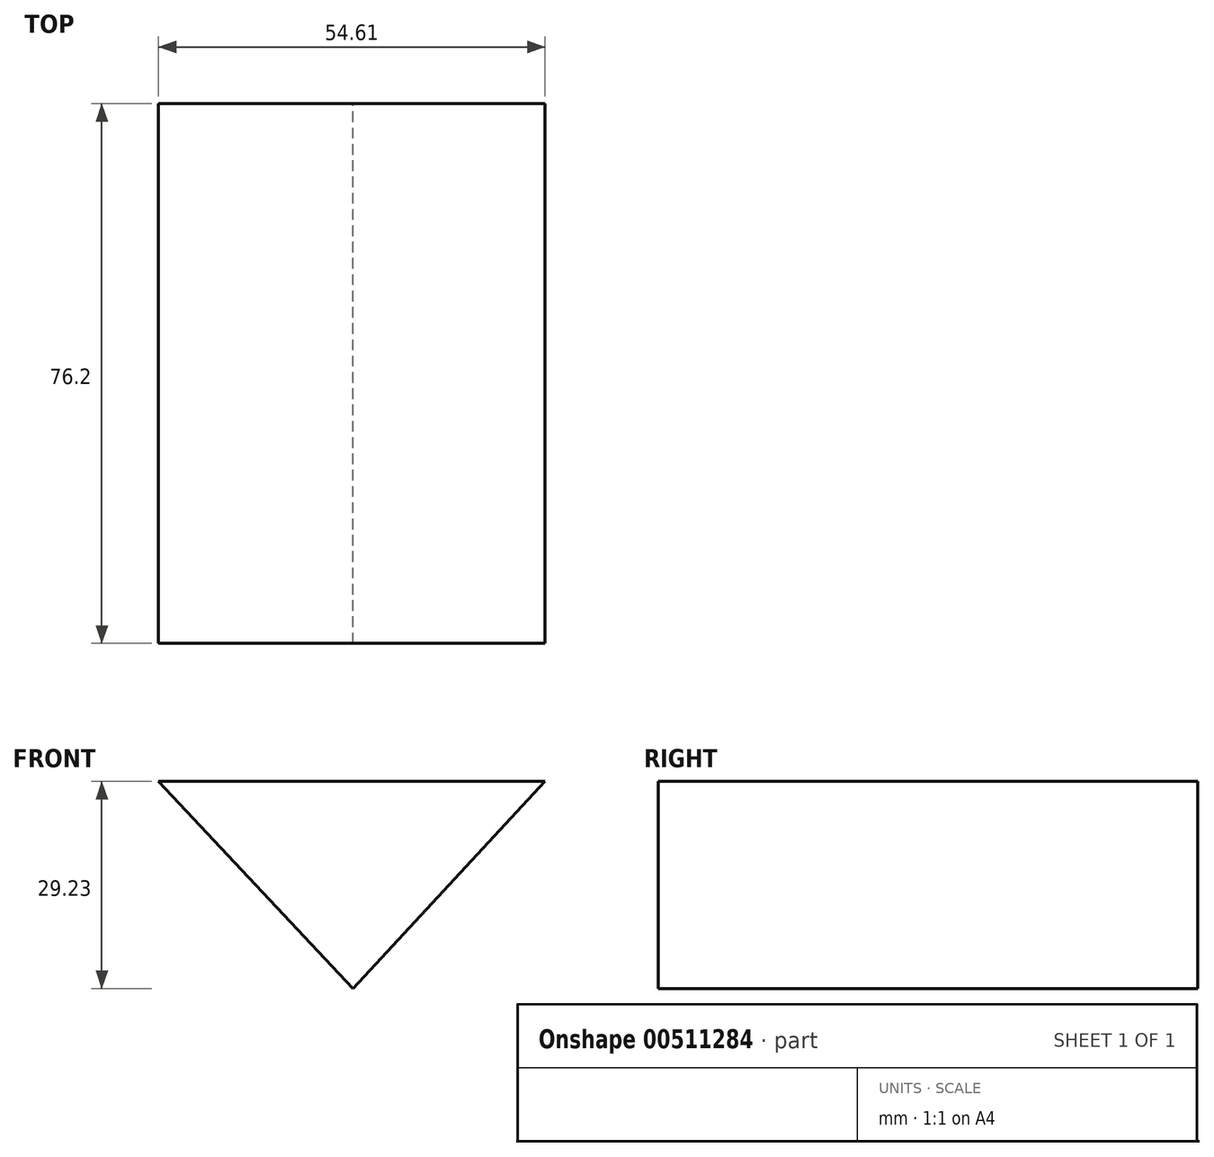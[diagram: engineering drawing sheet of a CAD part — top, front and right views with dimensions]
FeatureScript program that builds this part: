
annotation { "Feature Type Name" : "Feature", "Feature Type Description" : "" }
export const myFeature = defineFeature(function(context is Context, id is Id, definition is map)
    precondition{}
    {
        {
            var Q0;
            Q0=qCreatedBy(makeId("Front.planeOp"),FACE);
            var sketch = newSketch(context, id + "F0", { "sketchPlane" : qUnion([Q0])});
            skLineSegment(sketch, "E0", {"start": v(-37.83, 26.72) * mm, "end": v(16.78, 26.72) * mm});
            skLineSegment(sketch, "E1", {"start": v(16.78, 26.72) * mm, "end": v(-10.34, -2.51) * mm});
            skLineSegment(sketch, "E2", {"start": v(-10.34, -2.51) * mm, "end": v(-37.83, 26.72) * mm});
            skSolve(sketch);
        }
        {
            var Q0;
            Q0 = qSketchRegion(id + "F0", true);
            extrude(context, id + "F1", {"entities" : qUnion([Q0]), "depth" : 76.2 * mm});
        }
    });
